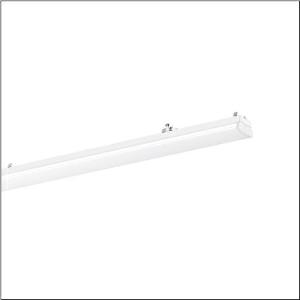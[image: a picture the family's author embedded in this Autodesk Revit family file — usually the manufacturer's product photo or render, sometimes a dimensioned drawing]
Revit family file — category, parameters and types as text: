
# Revit family: licross_r__21_recessed_opal_ho_52tl1dmn4e5m_024b
name_source: partatom
category: Lighting Fixtures
units: mm (PartAtom-declared; Revit-internal decimal feet)

## family parameters
Cut with Voids When Loaded = No
Host = Face
Light Source = No
Part Type = Normal
Room Calculation Point = No
Round Connector Dimension = Use Diameter
Shared = No

## types (1)
- --- (1 x LED, 14660 lm, 83.1 W, 4000K)
    Apparent Load = 83 VA
    CIE Flux Codes = 44 73 91 87 100
    Color Rendering = 80
    Color Temperature = 4000K
    Default Elevation = 1800 mm
    Description = Licross® 21 recessed opal HO, luminaire insert, of sheet steel, galvanised, coil coated, white, length: 1.500mm, width: 66mm, height: 67mm, LED rated luminous flux: 14.660lm, light colour: 840, control gear: ON/OFF Multilumen, with plug, 3-pole, with phase selection, mains connection: 220..240V, AC, 50/60Hz, rated input power: 83W, halogen-free wiring, primary optical cover: cover, of PMMA, light emission: direct with ceiling illumination distribution, primary light characteristic: symmetric, protection rating (complete): IP40, insulation class (complete): insulation class I (protective earthing), certification: CE, ENEC, VDE, UKCA, protection symbol: D if used in an environment without relevant dust loads with corresponding accessories, impact resistance: IK06, permissible ambient temperature for indoor applications: -35..+30°C, corresponds to IFS (International Featured Standards) requirements for safety and quality in the food industry, reducing of maximum allowable ambient temperature of 5°C with ceiling mounting, LABS conformity tested according to VDMA 24364:2018-05, packaging unit: 1 piece
    Height = 83 mm
    Lamp = 1 x LED
    Lamp Light Flux = 14660 lm
    Lamp Power = 83.1 W
    Lamp count = 1
    Length = 1500 mm
    Luminous efficacy = 176 lm/W
    Manufacturer = Siteco
    ModVariant = No
    Model = 52TL1DMN4E5M
    Mounting Place = Ceiling
    Mounting Type = Pendant
    Number of Poles = 1
    OnlyDefault = Yes
    Power Factor = 1
    Product Name = Licross® 21 recessed opal HO
    Product group = luminaire insert
    ProductGroupID = 901
    Protection Class = Protection class I
    Protection Degree = IP 40
    RLX_Detail_Level = 1
    RLX_Emergency_Light_Flux = 0 lm
    RLX_Emergency_Type = 0
    RLX_Emergency_Type_DB = No
    RlxData = <blob elided: 24749 chars, md5=075677a9>
    Socket = socket
    Standby Power = 0 W
    System Light Flux = 14660 lm
    System Power = 83 W
    Type Comments = factory setting: luminous flux: 100 % | (A | C | E) | 195 mA
    Type Image = l_1313666.jpg
    URL = http://relux.com
    VarID = @adj_023349
    Voltage = 0 V
    Weight = 0.00 kg
    Width = 76 mm

## geometry (parser evidence)
native form markers: Blend x4, Sweep x14
no freeform markers — native parametric forms only
